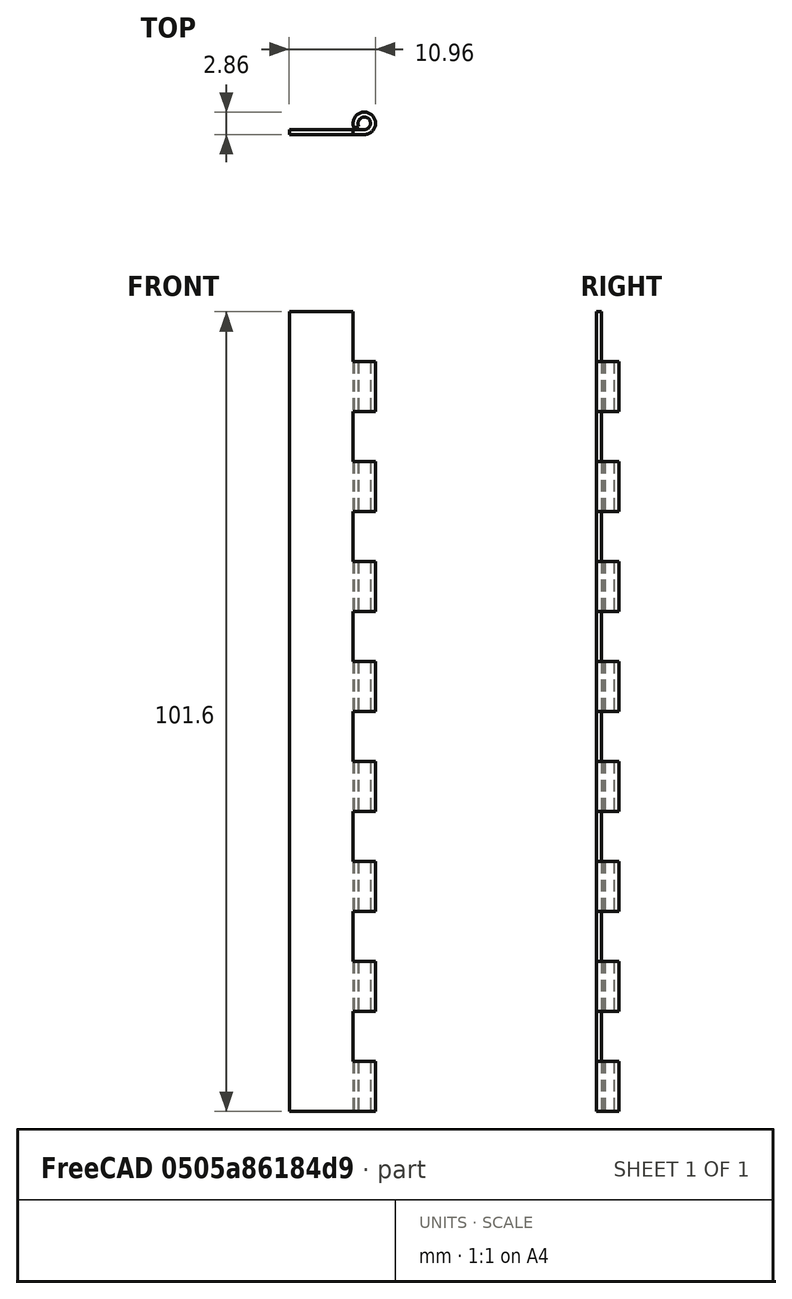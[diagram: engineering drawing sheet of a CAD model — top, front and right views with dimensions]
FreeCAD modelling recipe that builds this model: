
FCSTD DOCUMENT  (FreeCAD 0.19R24267 (Git))
Label: hinge_l-4
License: All rights reserved
LicenseURL: http://en.wikipedia.org/wiki/All_rights_reserved
objects: Part::Feature×1, Sketcher::SketchObject×1, Part::Extrusion×1, Part::Cut×1
note: 4 computed .brp shape members not serialized (recipe doc carries the construction recipe); baked Part::Feature solids carry a one-line shape summary decoded from their .brp

FEATURE [Part::Feature] Solid002
  shape: bbox 10.95 x 2.858 x 304.8 mm, 244 faces (baked)
FEATURE [Sketcher::SketchObject] Sketch
  FullyConstrained = false
  MapMode = 5
  Placement = pos=(0,0,152.4) rot=(0,0,1;0rad)
  Support = -> [Solid002]
  sketch-geometry (4):
    g0: LineSegment StartX=-10.6977 StartY=3.40063 StartZ=0 EndX=3.33717 EndY=3.40063 EndZ=0
    g1: LineSegment StartX=3.33717 StartY=3.40063 StartZ=0 EndX=3.33717 EndY=-2.84486 EndZ=0
    g2: LineSegment StartX=3.33717 StartY=-2.84486 StartZ=0 EndX=-10.6977 EndY=-2.84486 EndZ=0
    g3: LineSegment StartX=-10.6977 StartY=-2.84486 StartZ=0 EndX=-10.6977 EndY=3.40063 EndZ=0
  constraints (8):
    c: Coincident(g0,g1)
    c: Coincident(g1,g2)
    c: Coincident(g2,g3)
    c: Coincident(g3,g0)
    c: Horizontal(g0)
    c: Horizontal(g2)
    c: Vertical(g1)
    c: Vertical(g3)
FEATURE [Part::Extrusion] Extrude
  Base = -> Sketch
  Dir = (0,0,1)
  DirMode = 2
  FaceMakerClass = Part::FaceMakerBullseye
  LengthFwd = 0
  LengthRev = 203.2
  Solid = true
  Symmetric = false
FEATURE [Part::Cut] Cut
  Base = -> Solid002
  Tool = -> Extrude
